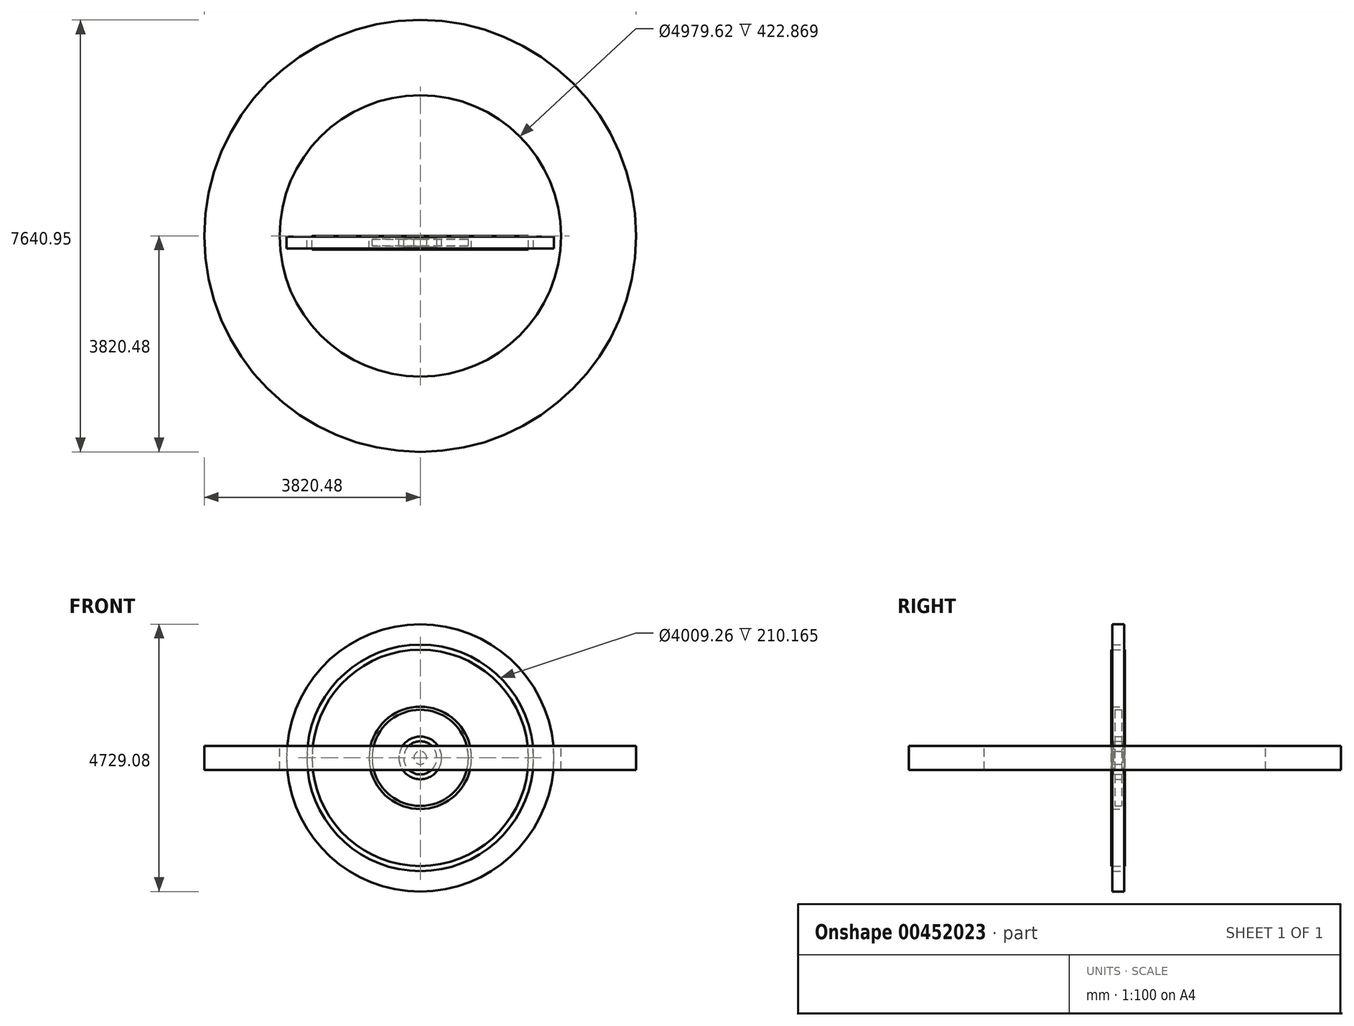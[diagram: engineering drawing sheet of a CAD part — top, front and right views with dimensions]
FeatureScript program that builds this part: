
annotation { "Feature Type Name" : "Feature", "Feature Type Description" : "" }
export const myFeature = defineFeature(function(context is Context, id is Id, definition is map)
    precondition{}
    {
        {
            var Q0;
            Q0=qCreatedBy(makeId("Top.planeOp"),FACE);
            var sketch = newSketch(context, id + "F0", { "sketchPlane" : qUnion([Q0])});
            skLineSegment(sketch, "E0.bottom", {"start": v(113.82, -80.35) * mm, "end": v(292.8, -80.35) * mm});
            skLineSegment(sketch, "E0.top", {"start": v(113.82, 80.35) * mm, "end": v(292.8, 80.35) * mm});
            skLineSegment(sketch, "E0.left", {"start": v(113.82, -80.35) * mm, "end": v(113.82, 80.35) * mm});
            skLineSegment(sketch, "E0.right", {"start": v(292.8, -80.35) * mm, "end": v(292.8, 80.35) * mm});
            skPoint(sketch, "E0.middle", {"position": v(203.31, 0) * mm});
            skLineSegment(sketch, "E1", {"start": v(0, 139.47) * mm, "end": v(0, -110.73) * mm, "construction": true});
            skSolve(sketch);
        }
        {
            var Q0;
            Q0 = qSketchRegion(id + "F0", true);
            var Q1;
            Q1=sQuery(id+"F0.wireOp",EDGE,"E1");
            revolve(context, id + "F1", {"entities" : qUnion([Q0]), "axis" : qUnion([Q1]), "revolveType" : RevolveType.FULL});
        }
        {
            var Q0;
            Q0=qCreatedBy(makeId("Top.planeOp"),FACE);
            var sketch = newSketch(context, id + "F2", { "sketchPlane" : qUnion([Q0])});
            skLineSegment(sketch, "E2.bottom", {"start": v(377.81, -59.7) * mm, "end": v(850.95, -59.7) * mm});
            skLineSegment(sketch, "E2.top", {"start": v(377.81, 59.7) * mm, "end": v(850.95, 59.7) * mm});
            skLineSegment(sketch, "E2.left", {"start": v(377.81, -59.7) * mm, "end": v(377.81, 59.7) * mm});
            skLineSegment(sketch, "E2.right", {"start": v(850.95, -59.7) * mm, "end": v(850.95, 59.7) * mm});
            skPoint(sketch, "E2.middle", {"position": v(614.38, 0) * mm});
            skLineSegment(sketch, "E3.0", {"start": v(0, 139.47) * mm, "end": v(0, -110.73) * mm});
            skSolve(sketch);
        }
        {
            var Q0;
            Q0 = qSketchRegion(id + "F2", true);
            var Q1;
            Q1=sQuery(id+"F0.wireOp",EDGE,"E1");
            revolve(context, id + "F3", {"entities" : qUnion([Q0]), "axis" : qUnion([Q1]), "revolveType" : RevolveType.FULL});
        }
        {
            var Q0;
            Q0=qCreatedBy(makeId("Top.planeOp"),FACE);
            var sketch = newSketch(context, id + "F4", { "sketchPlane" : qUnion([Q0])});
            skLineSegment(sketch, "E4.bottom", {"start": v(905.63, -119.33) * mm, "end": v(1913.11, -119.33) * mm});
            skLineSegment(sketch, "E4.top", {"start": v(905.63, 119.33) * mm, "end": v(1913.11, 119.33) * mm});
            skLineSegment(sketch, "E4.left", {"start": v(905.63, -119.33) * mm, "end": v(905.63, 119.33) * mm});
            skLineSegment(sketch, "E4.right", {"start": v(1913.11, -119.33) * mm, "end": v(1913.11, 119.33) * mm});
            skPoint(sketch, "E4.middle", {"position": v(1409.37, 0) * mm});
            skLineSegment(sketch, "E5.0", {"start": v(0, 139.47) * mm, "end": v(0, -110.73) * mm});
            skSolve(sketch);
        }
        {
            var Q0;
            Q0 = qSketchRegion(id + "F4", true);
            var Q1;
            Q1=sQuery(id+"F0.wireOp",EDGE,"E1");
            revolve(context, id + "F5", {"entities" : qUnion([Q0]), "axis" : qUnion([Q1]), "revolveType" : RevolveType.FULL});
        }
        {
            var Q0;
            Q0=qCreatedBy(makeId("Top.planeOp"),FACE);
            var sketch = newSketch(context, id + "F6", { "sketchPlane" : qUnion([Q0])});
            skLineSegment(sketch, "E6.bottom", {"start": v(2364.54, 105.08) * mm, "end": v(2004.63, 105.08) * mm});
            skLineSegment(sketch, "E6.top", {"start": v(2364.54, -105.08) * mm, "end": v(2004.63, -105.08) * mm});
            skLineSegment(sketch, "E6.left", {"start": v(2364.54, 105.08) * mm, "end": v(2364.54, -105.08) * mm});
            skLineSegment(sketch, "E6.right", {"start": v(2004.63, 105.08) * mm, "end": v(2004.63, -105.08) * mm});
            skPoint(sketch, "E6.middle", {"position": v(2184.58, 0) * mm});
            skLineSegment(sketch, "E7.0", {"start": v(0, 139.47) * mm, "end": v(0, -110.73) * mm});
            skSolve(sketch);
        }
        {
            var Q0;
            Q0 = qSketchRegion(id + "F6", true);
            var Q1;
            Q1=sQuery(id+"F0.wireOp",EDGE,"E1");
            revolve(context, id + "F7", {"entities" : qUnion([Q0]), "axis" : qUnion([Q1]), "revolveType" : RevolveType.FULL});
        }
        {
            var Q0;
            Q0=makeQuery(id+"F5.opRevolve","SWEPT_FACE",FACE,{"disambiguationData":[OSD([sQuery(id+"F4.wireOp",EDGE,"E4.top")])]});
            var sketch = newSketch(context, id + "F8", { "sketchPlane" : qUnion([Q0])});
            skLineSegment(sketch, "E8", {"start": v(0, 190.89) * mm, "end": v(0, -193.78) * mm, "construction": true});
            skLineSegment(sketch, "E9.bottom", {"start": v(-2489.8, -211.43) * mm, "end": v(-3820.48, -211.43) * mm});
            skLineSegment(sketch, "E9.top", {"start": v(-2489.8, 211.43) * mm, "end": v(-3820.48, 211.43) * mm});
            skLineSegment(sketch, "E9.left", {"start": v(-2489.8, -211.43) * mm, "end": v(-2489.8, 211.43) * mm});
            skLineSegment(sketch, "E9.right", {"start": v(-3820.48, -211.43) * mm, "end": v(-3820.48, 211.43) * mm});
            skPoint(sketch, "E9.middle", {"position": v(-3155.14, 0) * mm});
            skSolve(sketch);
        }
        {
            var Q0;
            Q0 = qSketchRegion(id + "F8", true);
            var Q1;
            Q1=sQuery(id+"F8.wireOp",EDGE,"E8");
            revolve(context, id + "F9", {"entities" : qUnion([Q0]), "axis" : qUnion([Q1]), "revolveType" : RevolveType.FULL});
        }
    });
